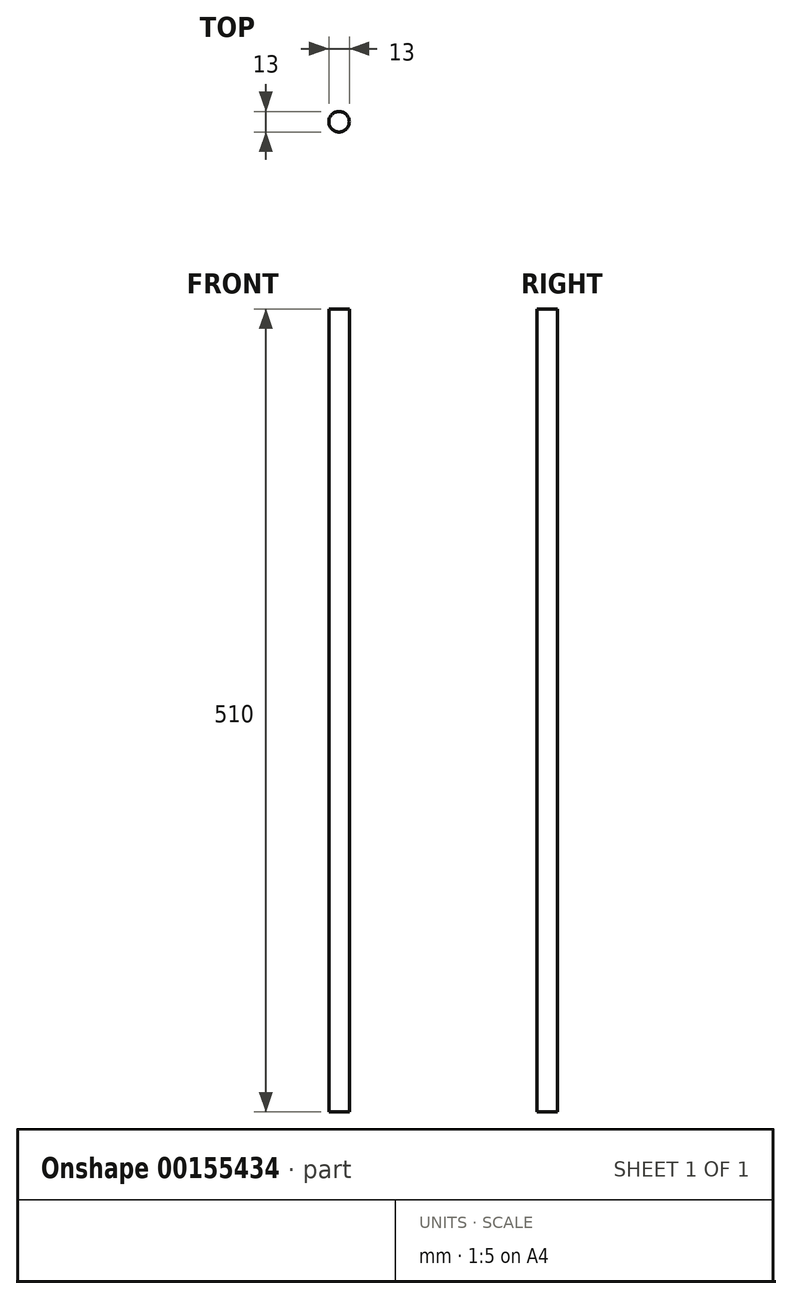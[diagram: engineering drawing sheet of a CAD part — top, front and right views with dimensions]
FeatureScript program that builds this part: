
annotation { "Feature Type Name" : "Feature", "Feature Type Description" : "" }
export const myFeature = defineFeature(function(context is Context, id is Id, definition is map)
    precondition{}
    {
        {
            var Q0;
            Q0=qCreatedBy(makeId("Top.planeOp"),FACE);
            var sketch = newSketch(context, id + "F0", { "sketchPlane" : qUnion([Q0])});
            skCircle(sketch, "E0", {"center": v(0, 0) * mm, "radius": 6.5 * mm});
            skSolve(sketch);
        }
        {
            var Q0;
            Q0 = qSketchRegion(id + "F0", true);
            extrude(context, id + "F1", {"entities" : qUnion([Q0]), "endBound" : BoundingType.SYMMETRIC, "depth" : 510 * mm});
        }
    });
